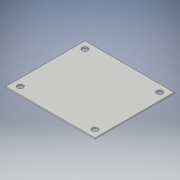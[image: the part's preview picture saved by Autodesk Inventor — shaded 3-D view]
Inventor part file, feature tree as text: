
AUTODESK INVENTOR PART (.ipt)
format: ipt  version: 2018 (Build 220112000, 112)  size: 104,960 bytes
history: native  units: in
note: dims shown in document units (in); Inventor stores cm internally (conversion verified against a paired STEP export)
features: extrude x2, sketch x2
ambient origin geometry x8: Origin, YZ Plane, XZ Plane, XY Plane, X Axis, Y Axis, Z Axis, Center Point
bodies: Solid1 (feature_tree)
feature tree (4):
  extrude  "Extrusion1"  Depth=2.1654in
  extrude  "Extrusion2"  Depth=0.031in
  sketch  "Sketch1"  dims[d0=2.4409in d1=2.1654in]
  sketch  "Sketch2"  dims[d2=0.031in d3=0.0in d4=0.1575in d5=0.1575in d6=0.1575in d7=0.1575in d8=0.0in d9=0.0in]
